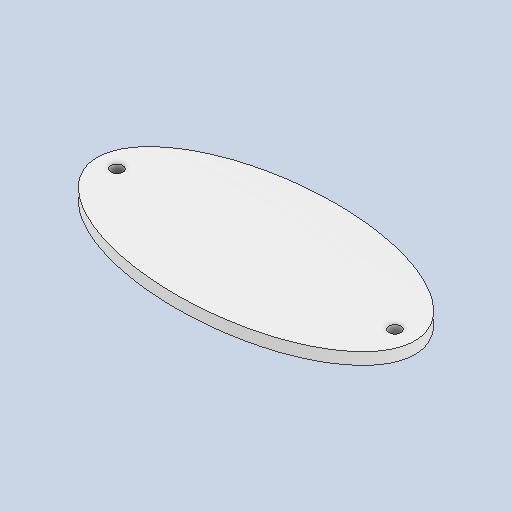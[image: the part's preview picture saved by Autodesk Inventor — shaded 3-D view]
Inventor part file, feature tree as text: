
AUTODESK INVENTOR PART (.ipt)
format: ipt  version: 2022 (Build 260153000, 153)  size: 98,304 bytes
history: native  units: in
note: dims shown in document units (in); Inventor stores cm internally (conversion verified against a paired STEP export)
features: extrude x1, sketch x1
ambient origin geometry x8: Origin, YZ Plane, XZ Plane, XY Plane, X Axis, Y Axis, Z Axis, Center Point
bodies: Solid1 (feature_tree)
feature tree (2):
  extrude  "Extrusion1"  [1 undecoded]
  sketch  "Sketch1"  dims[d6=0.1181in d7=0.0in]
note: 1 required parameter value undecoded (feature->parameter linkage not recoverable at this tier; creation-order binding heuristic only, values carry confidence <= 0.55)
